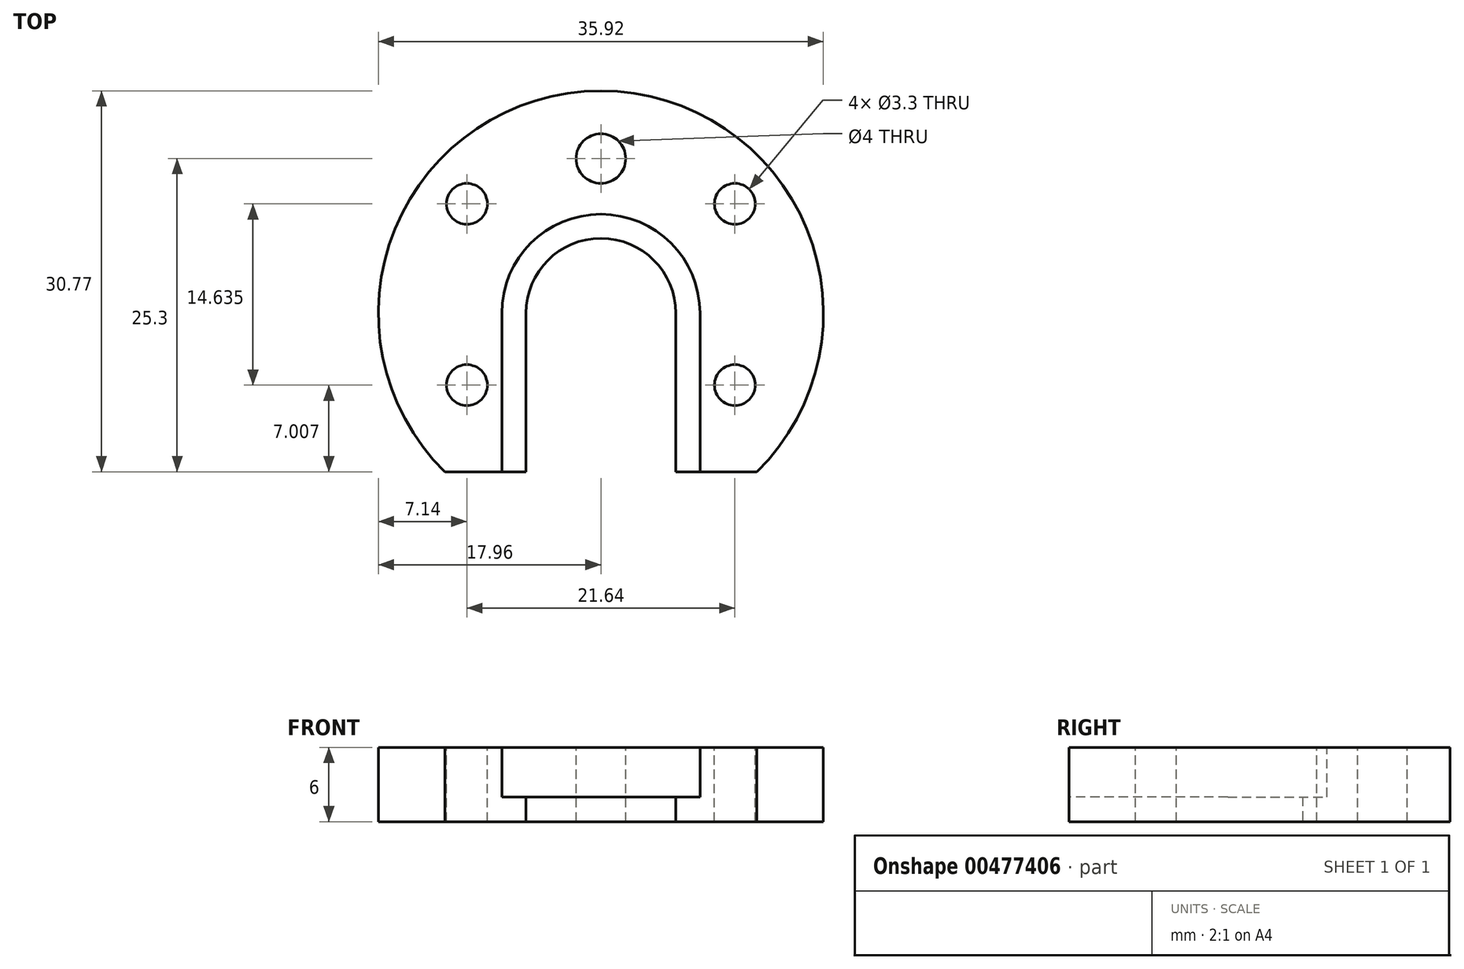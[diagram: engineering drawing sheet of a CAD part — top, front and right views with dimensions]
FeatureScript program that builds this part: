
annotation { "Feature Type Name" : "Feature", "Feature Type Description" : "" }
export const myFeature = defineFeature(function(context is Context, id is Id, definition is map)
    precondition{}
    {
        {
            var Q0;
            Q0=qCreatedBy(makeId("Top.planeOp"),FACE);
            var sketch = newSketch(context, id + "F0", { "sketchPlane" : qUnion([Q0])});
            skCircle(sketch, "E0", {"center": v(0, 0) * mm, "radius": 17.97 * mm});
            skCircle(sketch, "E1", {"center": v(0, 0) * mm, "radius": 6.05 * mm});
            skLineSegment(sketch, "E2", {"start": v(-6.05, 0) * mm, "end": v(-6.05, -16.92) * mm});
            skLineSegment(sketch, "E3", {"start": v(0, 0) * mm, "end": v(6.05, 0) * mm});
            skLineSegment(sketch, "E4", {"start": v(6.05, 0) * mm, "end": v(6.05, -16.92) * mm});
            skLineSegment(sketch, "E5", {"start": v(-12.6, -12.8) * mm, "end": v(12.6, -12.8) * mm});
            skSolve(sketch);
        }
        {
            var Q0;
            {var subQ3=sQuery(id+"F0.wireOp",EDGE,"E5");var subQ8=sQuery(id+"F0.wireOp",EDGE,"E0");var subQ9=makeQuery(id+"F0.imprint","INTERSECT",VERTEX,{"disambiguationData":[OD(0.0)],"derivedFrom":[subQ8,subQ3]});Q0=makeQuery(id+"F0.imprint","IMPRINT",FACE,{"disambiguationData":[TD([[makeQuery(id+"F0.imprint","IMPRINT",EDGE,{"disambiguationData":[TD([[subQ9,1.0]])],"derivedFrom":subQ8}),1.0]])]});}
            extrude(context, id + "F1", {"entities" : qUnion([Q0]), "depth" : 6 * mm});
        }
        {
            var Q0;
            Q0=makeQuery(id+"F1.opExtrude","CAP_FACE",FACE,{"disambiguationData":[OSD([sQuery(id+"F0.wireOp",EDGE,"E0"),sQuery(id+"F0.wireOp",EDGE,"E1"),sQuery(id+"F0.wireOp",EDGE,"E2"),sQuery(id+"F0.wireOp",EDGE,"E4"),sQuery(id+"F0.wireOp",EDGE,"E5")])],"isStart":false});
            var sketch = newSketch(context, id + "F2", { "sketchPlane" : qUnion([Q0])});
            skCircle(sketch, "E6", {"center": v(0, 12.5) * mm, "radius": 2 * mm});
            skCircle(sketch, "E7", {"center": v(-10.82, 8.83) * mm, "radius": 1.65 * mm});
            skCircle(sketch, "E8", {"center": v(-10.82, -5.8) * mm, "radius": 1.65 * mm});
            skCircle(sketch, "E9", {"center": v(10.82, 8.83) * mm, "radius": 1.65 * mm});
            skCircle(sketch, "E10", {"center": v(10.82, -5.8) * mm, "radius": 1.65 * mm});
            skPoint(sketch, "E11.endSnap0", {"position": v(-9.32, -12.8) * mm});
            skLineSegment(sketch, "E12", {"start": v(8, 0) * mm, "end": v(8, -12.8) * mm});
            skLineSegment(sketch, "E13", {"start": v(-10.82, 8.83) * mm, "end": v(-10.82, -5.8) * mm});
            skLineSegment(sketch, "E14", {"start": v(10.82, 8.83) * mm, "end": v(10.82, -5.8) * mm});
            skSolve(sketch);
        }
        {
            var Q0;
            Q0 = qSketchRegion(id + "F2", true);
            extrude(context, id + "F3", {"entities" : qUnion([Q0]), "operationType" : NewBodyOperationType.REMOVE, "oppositeDirection" : true, "depth" : 25.4 * mm});
        }
        {
            var Q0;
            Q0=makeQuery(id+"F1.opExtrude","CAP_FACE",FACE,{"disambiguationData":[OSD([sQuery(id+"F0.wireOp",EDGE,"E0"),sQuery(id+"F0.wireOp",EDGE,"E1"),sQuery(id+"F0.wireOp",EDGE,"E2"),sQuery(id+"F0.wireOp",EDGE,"E4"),sQuery(id+"F0.wireOp",EDGE,"E5")])],"isStart":false});
            var sketch = newSketch(context, id + "F4", { "sketchPlane" : qUnion([Q0])});
            skCircle(sketch, "E15", {"center": v(0, 0) * mm, "radius": 8 * mm});
            skLineSegment(sketch, "E16", {"start": v(-8, 0) * mm, "end": v(-8, -12.8) * mm});
            skLineSegment(sketch, "E17", {"start": v(8, 0) * mm, "end": v(8, -12.8) * mm});
            skSolve(sketch);
        }
        {
            var Q0;
            {var subQ0=makeQuery(id+"F1.opExtrude","CAP_EDGE",EDGE,{"disambiguationData":[OSD([sQuery(id+"F0.wireOp",EDGE,"E1")])],"isStart":false});Q0=makeQuery(id+"F4.imprint","IMPRINT",FACE,{"disambiguationData":[TD([[makeQuery(id+"F4.imprint","IMPRINT",EDGE,{"derivedFrom":subQ0}),-1.0]])]});}
            var Q1;
            {var subQ0=sQuery(id+"F4.wireOp",EDGE,"E16");Q1=makeQuery(id+"F4.imprint","IMPRINT",FACE,{"disambiguationData":[TD([[makeQuery(id+"F4.imprint","IMPRINT",EDGE,{"derivedFrom":subQ0}),1.0]])]});}
            var Q2;
            {var subQ0=sQuery(id+"F4.wireOp",EDGE,"E17");Q2=makeQuery(id+"F4.imprint","IMPRINT",FACE,{"disambiguationData":[TD([[makeQuery(id+"F4.imprint","IMPRINT",EDGE,{"derivedFrom":subQ0}),-1.0]])]});}
            extrude(context, id + "F5", {"entities" : qUnion([Q0, Q1, Q2]), "operationType" : NewBodyOperationType.REMOVE, "oppositeDirection" : true, "depth" : 4 * mm});
        }
    });
